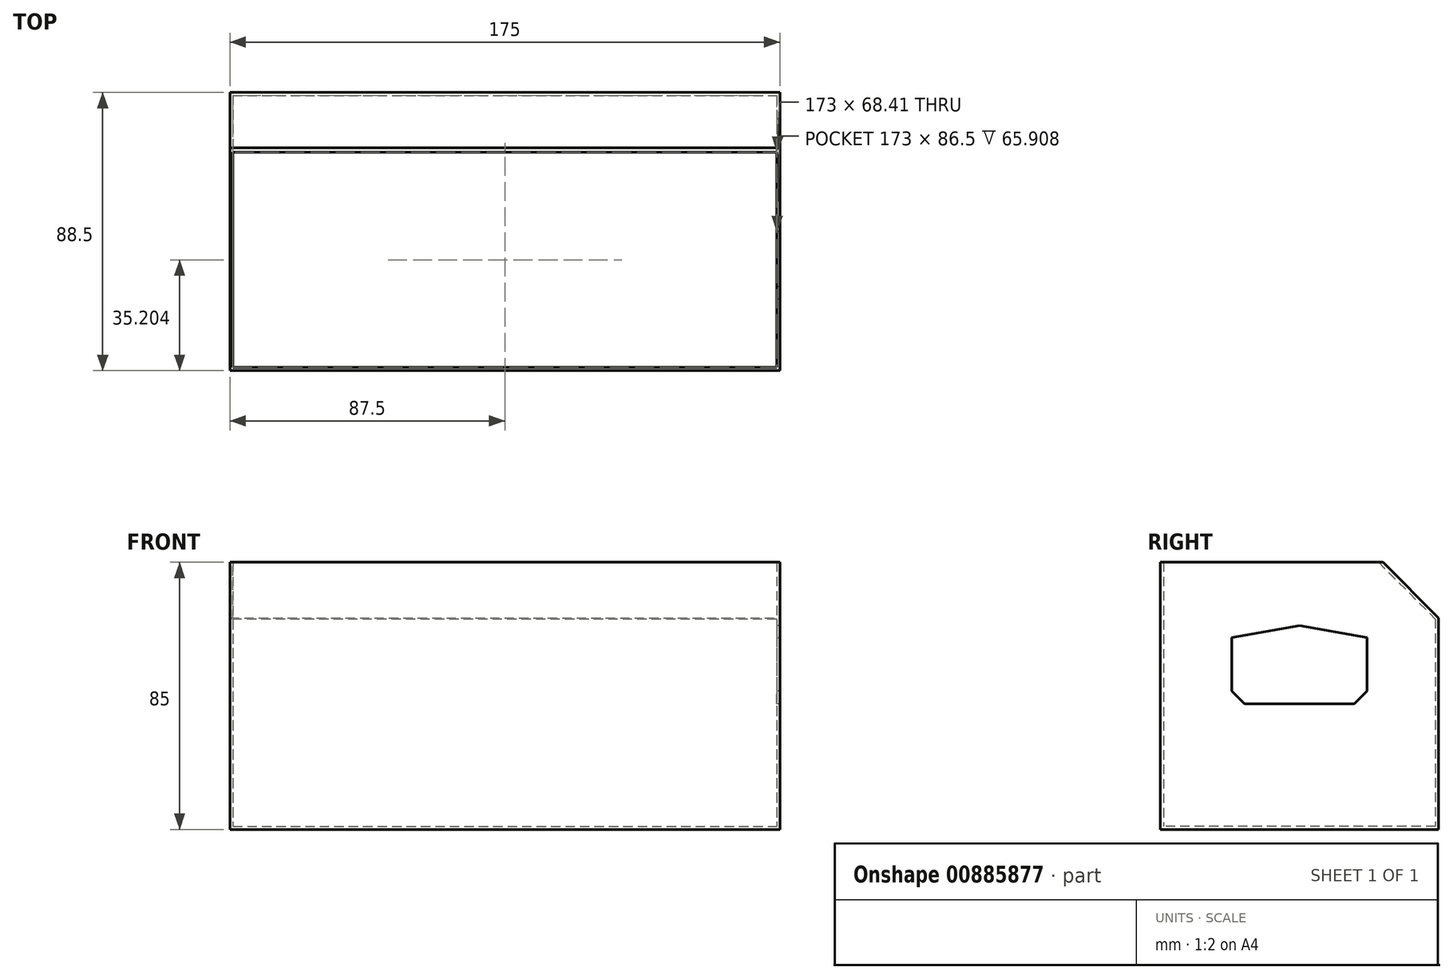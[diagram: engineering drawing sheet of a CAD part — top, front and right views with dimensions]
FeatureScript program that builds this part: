
annotation { "Feature Type Name" : "Feature", "Feature Type Description" : "" }
export const myFeature = defineFeature(function(context is Context, id is Id, definition is map)
    precondition{}
    {
        {
            var Q0;
            Q0=qCreatedBy(makeId("Top.planeOp"),FACE);
            var sketch = newSketch(context, id + "F0", { "sketchPlane" : qUnion([Q0])});
            skLineSegment(sketch, "E0.bottom", {"start": v(0, 0) * mm, "end": v(175, 0) * mm});
            skLineSegment(sketch, "E0.top", {"start": v(0, -88.5) * mm, "end": v(175, -88.5) * mm});
            skLineSegment(sketch, "E0.left", {"start": v(0, 0) * mm, "end": v(0, -88.5) * mm});
            skLineSegment(sketch, "E0.right", {"start": v(175, 0) * mm, "end": v(175, -88.5) * mm});
            skSolve(sketch);
        }
        {
            var Q0;
            Q0=qSketchRegion(id+"F0",true);
            extrude(context, id + "F1", {"entities" : qUnion([Q0]), "depth" : 85 * mm, "offsetDistance" : 25 * mm});
        }
        {
            var Q0;
            Q0=makeQuery(id+"F1.opExtrude","CAP_EDGE",EDGE,{"disambiguationData":[OSD([sQuery(id+"F0.wireOp",EDGE,"E0.bottom")])],"isStart":false});
            chamfer(context, id + "F2", {"entities" : qUnion([Q0]), "width" : 17.68 * mm, "tangentPropagation" : true});
        }
        {
            var Q0;
            Q0=makeQuery(id+"F1.opExtrude","CAP_FACE",FACE,{"disambiguationData":[OSD([sQuery(id+"F0.wireOp",EDGE,"E0.bottom"),sQuery(id+"F0.wireOp",EDGE,"E0.top"),sQuery(id+"F0.wireOp",EDGE,"E0.left"),sQuery(id+"F0.wireOp",EDGE,"E0.right")])],"isStart":false});
            shell(context, id + "F3", {"entities" : qUnion([Q0]), "thickness" : 1 * mm});
        }
        {
            var Q0;
            Q0=makeQuery(id+"F1.opExtrude","SWEPT_FACE",FACE,{"disambiguationData":[OSD([sQuery(id+"F0.wireOp",EDGE,"E0.right")])]});
            var sketch = newSketch(context, id + "F4", { "sketchPlane" : qUnion([Q0])});
            skLineSegment(sketch, "E1.bottom", {"start": v(-65.75, 65) * mm, "end": v(-22.75, 65) * mm});
            skLineSegment(sketch, "E1.top", {"start": v(-65.75, 40) * mm, "end": v(-22.75, 40) * mm});
            skLineSegment(sketch, "E1.left", {"start": v(-65.75, 65) * mm, "end": v(-65.75, 40) * mm});
            skLineSegment(sketch, "E1.right", {"start": v(-22.75, 65) * mm, "end": v(-22.75, 40) * mm});
            skSolve(sketch);
        }
        {
            var Q0;
            Q0=qSketchRegion(id+"F4",true);
            extrude(context, id + "F5", {"entities" : qUnion([Q0]), "operationType" : NewBodyOperationType.REMOVE, "oppositeDirection" : true, "depth" : 2 * mm, "offsetDistance" : 25 * mm});
        }
        {
            var Q0;
            Q0=makeQuery(id+"F5.boolean.opBoolean","COPY",EDGE,{"derivedFrom":makeQuery(id+"F5.opExtrude","SWEPT_EDGE",EDGE,{"disambiguationData":[OSD([sQuery(id+"F4.wireOp",EDGE,"E1.bottom"),sQuery(id+"F4.wireOp",EDGE,"E1.left")])]})});
            var Q1;
            Q1=makeQuery(id+"F5.boolean.opBoolean","COPY",EDGE,{"derivedFrom":makeQuery(id+"F5.opExtrude","SWEPT_EDGE",EDGE,{"disambiguationData":[OSD([sQuery(id+"F4.wireOp",EDGE,"E1.bottom"),sQuery(id+"F4.wireOp",EDGE,"E1.right")])]})});
            chamfer(context, id + "F6", {"entities" : qUnion([Q0, Q1]), "chamferType" : ChamferType.OFFSET_ANGLE, "width" : 4 * mm, "oppositeDirection" : false, "angle" : 80 * degree, "tangentPropagation" : true});
        }
        {
            var Q0;
            Q0=makeQuery(id+"F5.boolean.opBoolean","COPY",EDGE,{"derivedFrom":makeQuery(id+"F5.opExtrude","SWEPT_EDGE",EDGE,{"disambiguationData":[OSD([sQuery(id+"F4.wireOp",EDGE,"E1.top"),sQuery(id+"F4.wireOp",EDGE,"E1.left")])]})});
            var Q1;
            Q1=makeQuery(id+"F5.boolean.opBoolean","COPY",EDGE,{"derivedFrom":makeQuery(id+"F5.opExtrude","SWEPT_EDGE",EDGE,{"disambiguationData":[OSD([sQuery(id+"F4.wireOp",EDGE,"E1.top"),sQuery(id+"F4.wireOp",EDGE,"E1.right")])]})});
            chamfer(context, id + "F7", {"entities" : qUnion([Q0, Q1]), "width" : 4 * mm, "tangentPropagation" : true});
        }
    });
